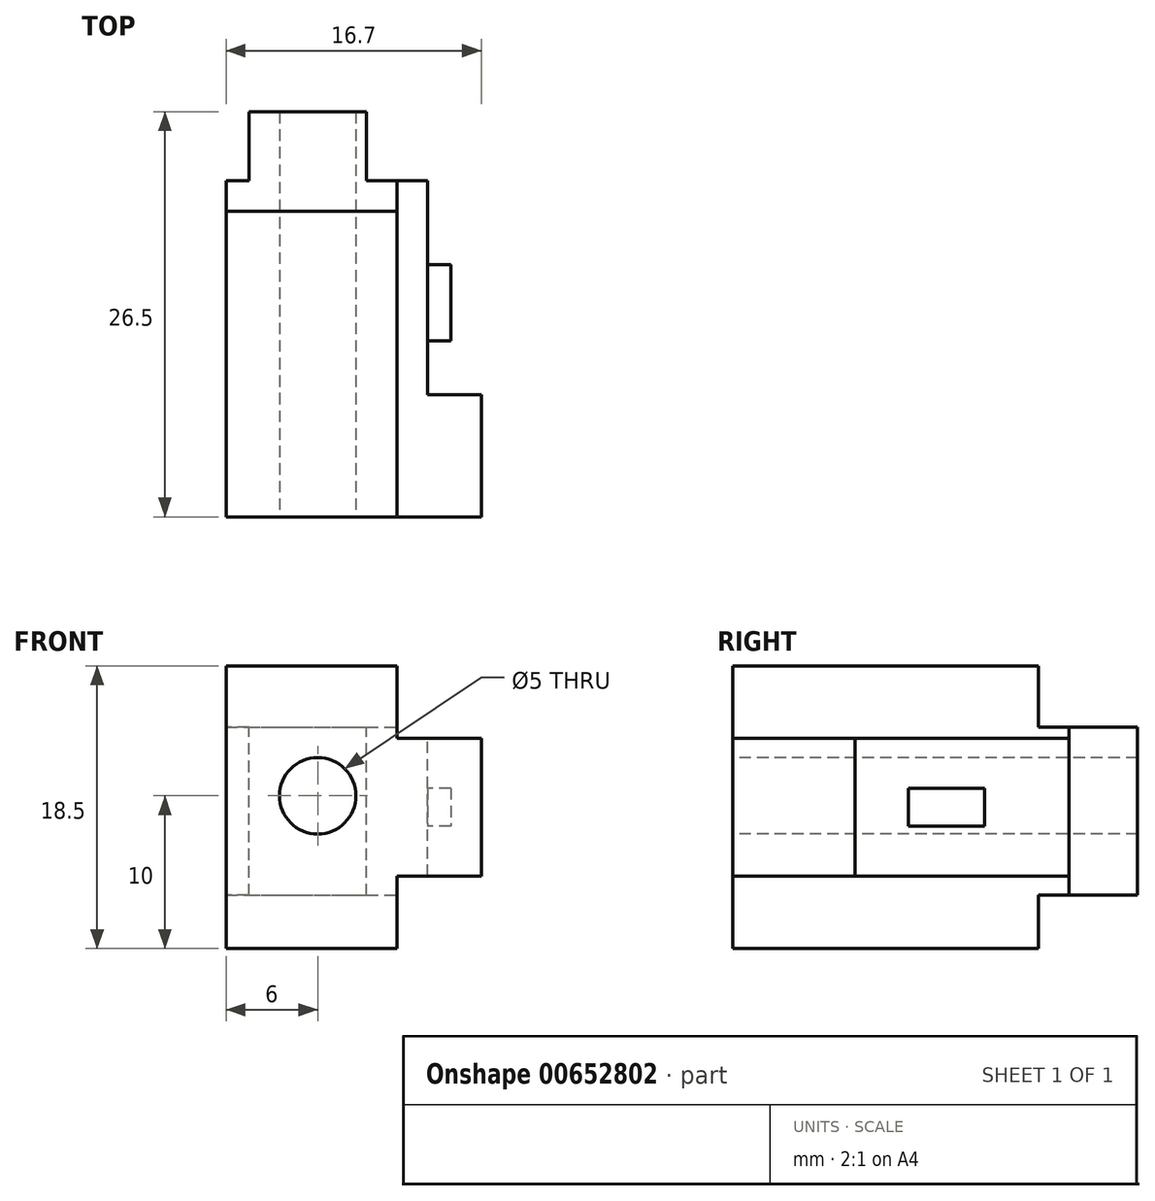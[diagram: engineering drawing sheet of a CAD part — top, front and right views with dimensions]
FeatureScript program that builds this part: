
annotation { "Feature Type Name" : "Feature", "Feature Type Description" : "" }
export const myFeature = defineFeature(function(context is Context, id is Id, definition is map)
    precondition{}
    {
        {
            var Q0;
            Q0=qCreatedBy(makeId("Front.planeOp"),FACE);
            var sketch = newSketch(context, id + "F0", { "sketchPlane" : qUnion([Q0])});
            skLineSegment(sketch, "E0.bottom", {"start": v(-6.6, 9.25) * mm, "end": v(6.6, 9.25) * mm});
            skLineSegment(sketch, "E0.top", {"start": v(-6.6, -9.25) * mm, "end": v(6.6, -9.25) * mm});
            skLineSegment(sketch, "E0.left", {"start": v(-6.6, 9.25) * mm, "end": v(-6.6, -9.25) * mm});
            skLineSegment(sketch, "E0.right", {"start": v(6.6, 9.25) * mm, "end": v(6.6, -9.25) * mm});
            skPoint(sketch, "E0.middle", {"position": v(0, 0) * mm});
            skSolve(sketch);
        }
        {
            var Q0;
            Q0 = qSketchRegion(id + "F0", true);
            extrude(context, id + "F1", {"entities" : qUnion([Q0]), "depth" : 26.5 * mm, "offsetDistance" : 25 * mm});
        }
        {
            var Q0;
            Q0=makeQuery(id+"F1.opExtrude","SWEPT_FACE",FACE,{"disambiguationData":[OSD([sQuery(id+"F0.wireOp",EDGE,"E0.bottom")])]});
            var sketch = newSketch(context, id + "F2", { "sketchPlane" : qUnion([Q0])});
            skLineSegment(sketch, "E1.bottom", {"start": v(6.6, 0) * mm, "end": v(2.6, 0) * mm});
            skLineSegment(sketch, "E1.top", {"start": v(6.6, -4.5) * mm, "end": v(2.6, -4.5) * mm});
            skLineSegment(sketch, "E1.left", {"start": v(6.6, 0) * mm, "end": v(6.6, -4.5) * mm});
            skLineSegment(sketch, "E1.right", {"start": v(2.6, 0) * mm, "end": v(2.6, -4.5) * mm});
            skLineSegment(sketch, "E2.bottom", {"start": v(-6.6, 0) * mm, "end": v(-5.1, 0) * mm});
            skLineSegment(sketch, "E2.top", {"start": v(-6.6, -4.5) * mm, "end": v(-5.1, -4.5) * mm});
            skLineSegment(sketch, "E2.left", {"start": v(-6.6, 0) * mm, "end": v(-6.6, -4.5) * mm});
            skLineSegment(sketch, "E2.right", {"start": v(-5.1, 0) * mm, "end": v(-5.1, -4.5) * mm});
            skSolve(sketch);
        }
        {
            var Q0;
            Q0 = qSketchRegion(id + "F2", true);
            extrude(context, id + "F3", {"entities" : qUnion([Q0]), "operationType" : NewBodyOperationType.REMOVE, "endBound" : BoundingType.THROUGH_ALL, "oppositeDirection" : true, "depth" : 25 * mm, "offsetDistance" : 25 * mm});
        }
        {
            var Q0;
            Q0=makeQuery(id+"F1.opExtrude","SWEPT_FACE",FACE,{"disambiguationData":[OSD([sQuery(id+"F0.wireOp",EDGE,"E0.right")])]});
            var sketch = newSketch(context, id + "F4", { "sketchPlane" : qUnion([Q0])});
            skLineSegment(sketch, "E3.bottom", {"start": v(-10, 1.25) * mm, "end": v(-15, 1.25) * mm});
            skLineSegment(sketch, "E3.top", {"start": v(-10, -1.25) * mm, "end": v(-15, -1.25) * mm});
            skLineSegment(sketch, "E3.left", {"start": v(-10, 1.25) * mm, "end": v(-10, -1.25) * mm});
            skLineSegment(sketch, "E3.right", {"start": v(-15, 1.25) * mm, "end": v(-15, -1.25) * mm});
            skSolve(sketch);
        }
        {
            var Q0;
            Q0 = qSketchRegion(id + "F4", true);
            extrude(context, id + "F5", {"entities" : qUnion([Q0]), "operationType" : NewBodyOperationType.ADD, "depth" : 1.5 * mm, "offsetDistance" : 25 * mm});
        }
        {
            var Q0;
            Q0=makeQuery(id+"F1.opExtrude","SWEPT_FACE",FACE,{"disambiguationData":[OSD([sQuery(id+"F0.wireOp",EDGE,"E0.right")])]});
            var sketch = newSketch(context, id + "F6", { "sketchPlane" : qUnion([Q0])});
            skLineSegment(sketch, "E4.0", {"start": v(0, -9.25) * mm, "end": v(-4.5, -9.25) * mm});
            skLineSegment(sketch, "E5.bottom", {"start": v(0, -9.25) * mm, "end": v(-6.5, -9.25) * mm});
            skLineSegment(sketch, "E5.top", {"start": v(0, -5.75) * mm, "end": v(-6.5, -5.75) * mm});
            skLineSegment(sketch, "E5.left", {"start": v(0, -9.25) * mm, "end": v(0, -5.75) * mm});
            skLineSegment(sketch, "E5.right", {"start": v(-6.5, -9.25) * mm, "end": v(-6.5, -5.75) * mm});
            skLineSegment(sketch, "E6.bottom", {"start": v(0, 9.25) * mm, "end": v(-6.5, 9.25) * mm});
            skLineSegment(sketch, "E6.top", {"start": v(0, 5.25) * mm, "end": v(-6.5, 5.25) * mm});
            skLineSegment(sketch, "E6.left", {"start": v(0, 9.25) * mm, "end": v(0, 5.25) * mm});
            skLineSegment(sketch, "E6.right", {"start": v(-6.5, 9.25) * mm, "end": v(-6.5, 5.25) * mm});
            skSolve(sketch);
        }
        {
            var Q0;
            Q0 = qSketchRegion(id + "F6", true);
            extrude(context, id + "F7", {"entities" : qUnion([Q0]), "operationType" : NewBodyOperationType.REMOVE, "endBound" : BoundingType.THROUGH_ALL, "oppositeDirection" : true, "depth" : 25 * mm, "offsetDistance" : 25 * mm});
        }
        {
            var Q0;
            Q0=makeQuery(id+"F1.opExtrude","SWEPT_FACE",FACE,{"disambiguationData":[OSD([sQuery(id+"F0.wireOp",EDGE,"E0.bottom")])]});
            var sketch = newSketch(context, id + "F8", { "sketchPlane" : qUnion([Q0])});
            skLineSegment(sketch, "E7.bottom", {"start": v(6.6, -26.5) * mm, "end": v(10.1, -26.5) * mm});
            skLineSegment(sketch, "E7.top", {"start": v(6.6, -18.5) * mm, "end": v(10.1, -18.5) * mm});
            skLineSegment(sketch, "E7.left", {"start": v(6.6, -26.5) * mm, "end": v(6.6, -18.5) * mm});
            skLineSegment(sketch, "E7.right", {"start": v(10.1, -26.5) * mm, "end": v(10.1, -18.5) * mm});
            skSolve(sketch);
        }
        {
            var Q0;
            Q0 = qSketchRegion(id + "F8", true);
            var Q1;
            Q1=makeQuery(id+"F1.opExtrude","SWEPT_FACE",FACE,{"disambiguationData":[OSD([sQuery(id+"F0.wireOp",EDGE,"E0.top")])]});
            extrude(context, id + "F9", {"entities" : qUnion([Q0]), "operationType" : NewBodyOperationType.ADD, "endBound" : BoundingType.UP_TO_SURFACE, "oppositeDirection" : true, "depth" : 25 * mm, "endBoundEntityFace" : qUnion([Q1]), "offsetDistance" : 25 * mm});
        }
        {
            var Q0;
            Q0=makeQuery(id+"F9.boolean.opBoolean","MERGE",FACE,{"derivedFrom":[makeQuery(id+"F1.opExtrude","CAP_FACE",FACE,{"disambiguationData":[OSD([sQuery(id+"F0.wireOp",EDGE,"E0.bottom"),sQuery(id+"F0.wireOp",EDGE,"E0.top"),sQuery(id+"F0.wireOp",EDGE,"E0.left"),sQuery(id+"F0.wireOp",EDGE,"E0.right")])],"isStart":false}),makeQuery(id+"F9.opExtrude","SWEPT_FACE",FACE,{"disambiguationData":[OSD([sQuery(id+"F8.wireOp",EDGE,"E7.bottom")])]})]});
            var sketch = newSketch(context, id + "F10", { "sketchPlane" : qUnion([Q0])});
            skCircle(sketch, "E8", {"center": v(-0.6, 0.75) * mm, "radius": 2.5 * mm});
            skSolve(sketch);
        }
        {
            var Q0;
            Q0 = qSketchRegion(id + "F10", true);
            extrude(context, id + "F11", {"entities" : qUnion([Q0]), "operationType" : NewBodyOperationType.REMOVE, "endBound" : BoundingType.THROUGH_ALL, "oppositeDirection" : true, "depth" : 25 * mm, "offsetDistance" : 25 * mm});
        }
        {
            var Q0;
            Q0=makeQuery(id+"F9.boolean.opBoolean","MERGE",FACE,{"derivedFrom":[makeQuery(id+"F1.opExtrude","CAP_FACE",FACE,{"disambiguationData":[OSD([sQuery(id+"F0.wireOp",EDGE,"E0.bottom"),sQuery(id+"F0.wireOp",EDGE,"E0.top"),sQuery(id+"F0.wireOp",EDGE,"E0.left"),sQuery(id+"F0.wireOp",EDGE,"E0.right")])],"isStart":false}),makeQuery(id+"F9.opExtrude","SWEPT_FACE",FACE,{"disambiguationData":[OSD([sQuery(id+"F8.wireOp",EDGE,"E7.bottom")])]})]});
            var sketch = newSketch(context, id + "F12", { "sketchPlane" : qUnion([Q0])});
            skLineSegment(sketch, "E9.bottom", {"start": v(10.1, 4.5) * mm, "end": v(4.6, 4.5) * mm});
            skLineSegment(sketch, "E9.top", {"start": v(10.1, -4.5) * mm, "end": v(4.6, -4.5) * mm});
            skLineSegment(sketch, "E10.top", {"start": v(10.1, 9.25) * mm, "end": v(4.6, 9.25) * mm});
            skLineSegment(sketch, "E10.left", {"start": v(10.1, 4.5) * mm, "end": v(10.1, 9.25) * mm});
            skLineSegment(sketch, "E10.right", {"start": v(4.6, 4.5) * mm, "end": v(4.6, 9.25) * mm});
            skLineSegment(sketch, "E11.top", {"start": v(4.6, -9.25) * mm, "end": v(10.1, -9.25) * mm});
            skLineSegment(sketch, "E11.left", {"start": v(4.6, -4.5) * mm, "end": v(4.6, -9.25) * mm});
            skLineSegment(sketch, "E11.right", {"start": v(10.1, -4.5) * mm, "end": v(10.1, -9.25) * mm});
            skSolve(sketch);
        }
        {
            var Q0;
            Q0 = qSketchRegion(id + "F12", true);
            extrude(context, id + "F13", {"entities" : qUnion([Q0]), "operationType" : NewBodyOperationType.REMOVE, "endBound" : BoundingType.THROUGH_ALL, "oppositeDirection" : true, "depth" : 25 * mm, "offsetDistance" : 25 * mm});
        }
    });
